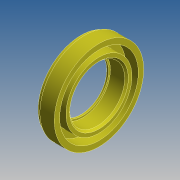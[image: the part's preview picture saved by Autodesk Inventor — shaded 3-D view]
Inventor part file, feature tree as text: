
AUTODESK INVENTOR PART (.ipt)
format: ipt  version: 2015 SP1 (Build 190203100, 203)  size: 235,008 bytes
history: native  units: mm
features: revolve x1, chamfer x1, sketch x1
ambient origin geometry x8: Origin, YZ Plane, XZ Plane, XY Plane, X Axis, Y Axis, Z Axis, Center Point
bodies: Solid1 (feature_tree)
feature tree (3):
  revolve  "Revolution1"  [1 undecoded]
  chamfer  "Chamfer1"  Distance=10.0mm
  sketch  "Sketch1"  dims[d0=49.8mm d1=47.8mm d2=10.0mm d3=1.0mm d4=2.0mm d5=30.7mm d6=1.0mm d7=3.0mm d8=3.0mm d9=3.0mm d10=10.0mm d11=90.0deg d12=1.0mm d13=2.0mm d14=45.0deg]
note: 1 required parameter value undecoded (feature->parameter linkage not recoverable at this tier; creation-order binding heuristic only, values carry confidence <= 0.55)
